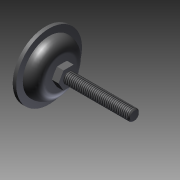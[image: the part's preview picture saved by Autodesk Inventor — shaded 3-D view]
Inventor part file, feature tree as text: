
AUTODESK INVENTOR PART (.ipt)
format: ipt  version: 2011 SP1 (Build 150282100, 282)  size: 137,216 bytes
history: native  units: mm
features: other x21, sketch x2, revolve x1, thread x1, extrude x1
ambient origin geometry x8: Origin, YZ Plane, XZ Plane, XY Plane, X Axis, Y Axis, Z Axis, Center Point
bodies: Solid1 (feature_tree)
feature tree (26):
  revolve  "Revolution1"  [1 undecoded]
  thread  "Thread1"  [1 undecoded]
  extrude  "Extrusion1"  [1 undecoded]
  other  "pad_to_dummy_XY"
  other  "pad_to_dummy_YZ"
  other  "pad_to_dummy_ZX"
  other  "pad_to_dummy_X"
  other  "pad_to_dummy_Y"
  other  "pad_to_dummy_Z"
  other  "pad_to_dummy_Center"
  other  "pad_to_nut_XY"
  other  "pad_to_nut_YZ"
  other  "pad_to_nut_ZX"
  other  "pad_to_nut_X"
  other  "pad_to_nut_Y"
  other  "pad_to_nut_Z"
  other  "pad_to_nut_Center"
  other  "pad_to_plate_XY"
  other  "pad_to_plate_YZ"
  other  "pad_to_plate_ZX"
  other  "pad_to_plate_X"
  other  "pad_to_plate_Y"
  other  "pad_to_plate_Z"
  other  "pad_to_plate_Center"
  sketch  "Sketch_1"  dims[d0=360.0deg d1=29.5095mm d2=0.0mm d3=3.5mm d4=0.0mm]
  sketch  "Sketch_2"  dims[d5=0.0mm]
note: 3 required parameter values undecoded (feature->parameter linkage not recoverable at this tier; creation-order binding heuristic only, values carry confidence <= 0.55)